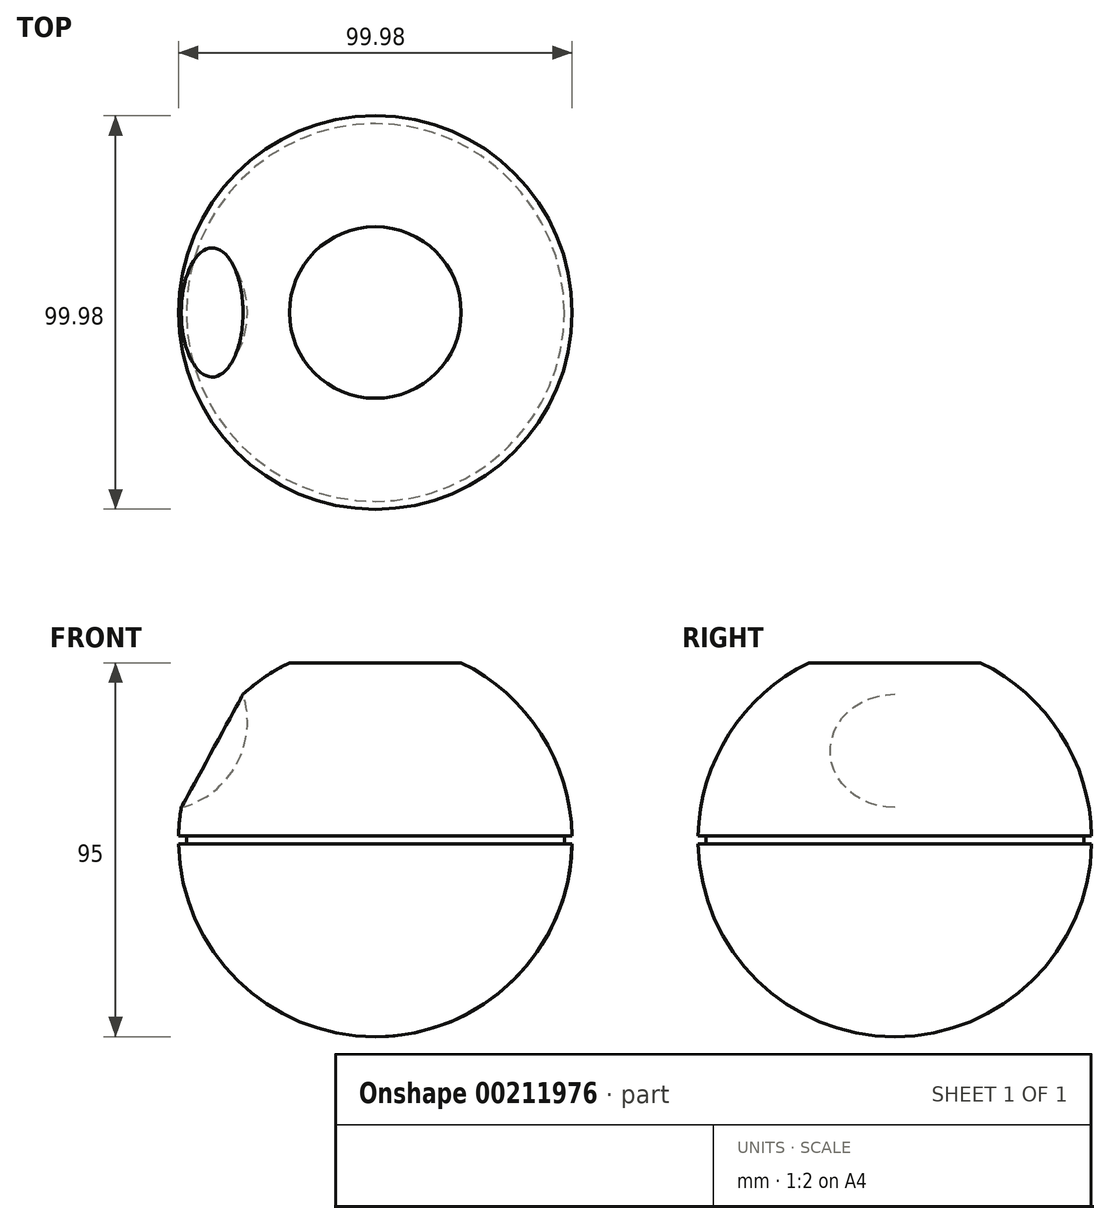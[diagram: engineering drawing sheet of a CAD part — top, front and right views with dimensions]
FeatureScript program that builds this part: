
annotation { "Feature Type Name" : "Feature", "Feature Type Description" : "" }
export const myFeature = defineFeature(function(context is Context, id is Id, definition is map)
    precondition{}
    {
        {
            var Q0;
            Q0=qCreatedBy(makeId("Front.planeOp"),FACE);
            var sketch = newSketch(context, id + "F0", { "sketchPlane" : qUnion([Q0])});
            skArc(sketch, "E0", {"start": v(0, 50) * mm, "mid": v(-50, 0) * mm, "end": v(0, -50) * mm});
            skLineSegment(sketch, "E1", {"start": v(0, 50) * mm, "end": v(0, -50) * mm});
            skSolve(sketch);
        }
        {
            var Q0;
            Q0=makeQuery(id+"F0.imprint","IMPRINT",FACE,{"disambiguationData":[TD([[makeQuery(id+"F0.imprint","IMPRINT",EDGE,{"derivedFrom":sQuery(id+"F0.wireOp",EDGE,"E0")}),1.0]])]});
            var Q1;
            Q1=sQuery(id+"F0.wireOp",EDGE,"E1");
            revolve(context, id + "F1", {"entities" : qUnion([Q0]), "axis" : qUnion([Q1]), "revolveType" : RevolveType.FULL});
        }
        {
            var Q0;
            Q0=qCreatedBy(makeId("Front.planeOp"),FACE);
            var sketch = newSketch(context, id + "F2", { "sketchPlane" : qUnion([Q0])});
            skArc(sketch, "E2", {"start": v(-55, 7.5) * mm, "mid": v(-32.5, 30) * mm, "end": v(-55, 52.5) * mm});
            skLineSegment(sketch, "E3", {"start": v(-55, 52.5) * mm, "end": v(-55, 7.5) * mm});
            skSolve(sketch);
        }
        {
            var Q0;
            Q0=makeQuery(id+"F2.imprint","IMPRINT",FACE,{"disambiguationData":[TD([[makeQuery(id+"F2.imprint","IMPRINT",EDGE,{"derivedFrom":sQuery(id+"F2.wireOp",EDGE,"E2")}),1.0]])]});
            var Q1;
            Q1=sQuery(id+"F2.wireOp",EDGE,"E3");
            revolve(context, id + "F3", {"operationType" : NewBodyOperationType.REMOVE, "entities" : qUnion([Q0]), "axis" : qUnion([Q1]), "revolveType" : RevolveType.FULL, "oppositeDirection" : true});
        }
        {
            var Q0;
            Q0=qCreatedBy(makeId("Front.planeOp"),FACE);
            var sketch = newSketch(context, id + "F4", { "sketchPlane" : qUnion([Q0])});
            skLineSegment(sketch, "E4.bottom", {"start": v(-48.3, 64.57) * mm, "end": v(49.85, 64.57) * mm});
            skLineSegment(sketch, "E4.top", {"start": v(-48.3, 45) * mm, "end": v(49.85, 45) * mm});
            skLineSegment(sketch, "E4.left", {"start": v(-48.3, 64.57) * mm, "end": v(-48.3, 45) * mm});
            skLineSegment(sketch, "E4.right", {"start": v(49.85, 64.57) * mm, "end": v(49.85, 45) * mm});
            skSolve(sketch);
        }
        {
            var Q0;
            Q0=makeQuery(id+"F4.imprint","IMPRINT",FACE,{"disambiguationData":[TD([[makeQuery(id+"F4.imprint","IMPRINT",EDGE,{"derivedFrom":sQuery(id+"F4.wireOp",EDGE,"E4.bottom")}),-1.0]])]});
            extrude(context, id + "F5", {"entities" : qUnion([Q0]), "operationType" : NewBodyOperationType.REMOVE, "oppositeDirection" : true, "depth" : 25 * mm, "hasSecondDirection" : true, "secondDirectionOppositeDirection" : false, "secondDirectionDepth" : 25 * mm});
        }
        {
            var Q0;
            Q0=qCreatedBy(makeId("Front.planeOp"),FACE);
            var sketch = newSketch(context, id + "F6", { "sketchPlane" : qUnion([Q0])});
            skLineSegment(sketch, "E5.bottom", {"start": v(-60.65, 0.95) * mm, "end": v(-48, 0.95) * mm});
            skLineSegment(sketch, "E5.top", {"start": v(-60.65, -1.05) * mm, "end": v(-48, -1.05) * mm});
            skLineSegment(sketch, "E5.left", {"start": v(-60.65, 0.95) * mm, "end": v(-60.65, -1.05) * mm});
            skLineSegment(sketch, "E5.right", {"start": v(-48, 0.95) * mm, "end": v(-48, -1.05) * mm});
            skLineSegment(sketch, "E6", {"start": v(0, 0) * mm, "end": v(0, 42.36) * mm, "construction": true});
            skSolve(sketch);
        }
        {
            var Q0;
            Q0 = qSketchRegion(id + "F6", true);
            var Q1;
            Q1=sQuery(id+"F6.wireOp",EDGE,"E6");
            revolve(context, id + "F7", {"operationType" : NewBodyOperationType.REMOVE, "entities" : qUnion([Q0]), "axis" : qUnion([Q1]), "revolveType" : RevolveType.FULL, "oppositeDirection" : true});
        }
    });
